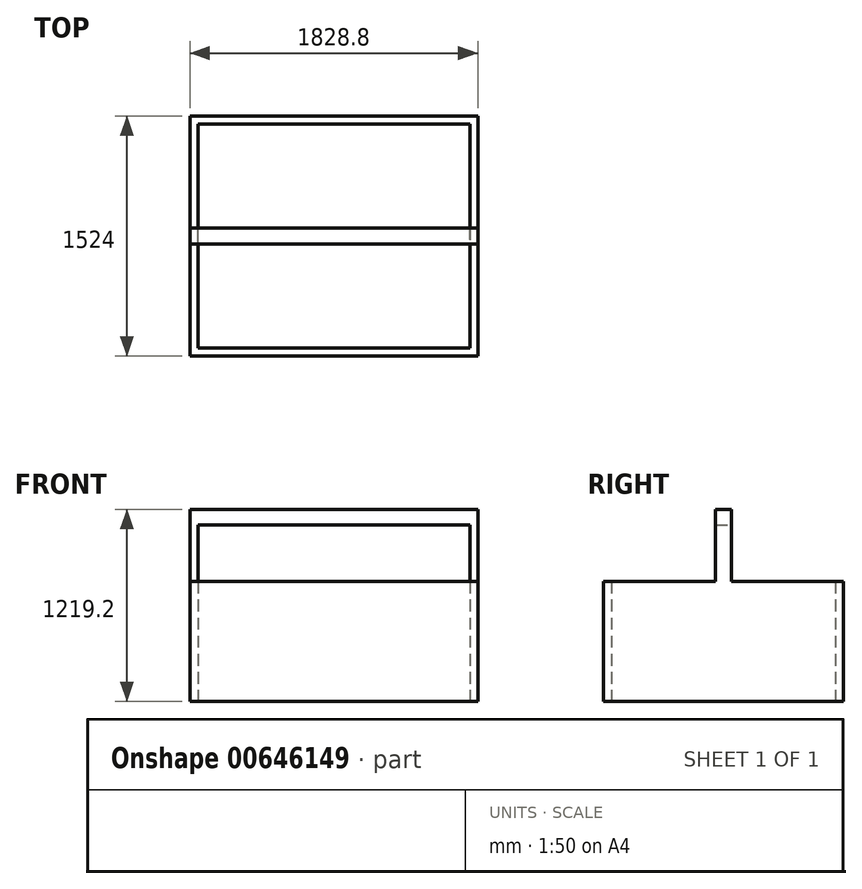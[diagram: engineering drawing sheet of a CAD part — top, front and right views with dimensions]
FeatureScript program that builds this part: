
annotation { "Feature Type Name" : "Feature", "Feature Type Description" : "" }
export const myFeature = defineFeature(function(context is Context, id is Id, definition is map)
    precondition{}
    {
        {
            var Q0;
            Q0=qCreatedBy(makeId("Top.planeOp"),FACE);
            var sketch = newSketch(context, id + "F0", { "sketchPlane" : qUnion([Q0])});
            skLineSegment(sketch, "E0.bottom", {"start": v(-610.33, -745.03) * mm, "end": v(1218.47, -745.03) * mm});
            skLineSegment(sketch, "E0.top", {"start": v(-610.33, 778.97) * mm, "end": v(1218.47, 778.97) * mm});
            skLineSegment(sketch, "E0.left", {"start": v(-610.33, -745.03) * mm, "end": v(-610.33, 778.97) * mm});
            skLineSegment(sketch, "E0.right", {"start": v(1218.47, -745.03) * mm, "end": v(1218.47, 778.97) * mm});
            skLineSegment(sketch, "E1.0", {"start": v(-559.53, 728.17) * mm, "end": v(1167.67, 728.17) * mm});
            skLineSegment(sketch, "E1.1", {"start": v(-559.53, -694.23) * mm, "end": v(-559.53, 728.17) * mm});
            skLineSegment(sketch, "E1.2", {"start": v(-559.53, -694.23) * mm, "end": v(1167.67, -694.23) * mm});
            skLineSegment(sketch, "E1.3", {"start": v(1167.67, -694.23) * mm, "end": v(1167.67, 728.17) * mm});
            skSolve(sketch);
        }
        {
            var Q0;
            Q0=makeQuery(id+"F0.imprint","IMPRINT",FACE,{"disambiguationData":[TD([[makeQuery(id+"F0.imprint","IMPRINT",EDGE,{"derivedFrom":sQuery(id+"F0.wireOp",EDGE,"E0.bottom")}),1.0]])]});
            extrude(context, id + "F1", {"entities" : qUnion([Q0]), "depth" : 762 * mm, "offsetDistance" : 25.4 * mm});
        }
        {
            var Q0;
            Q0=makeQuery(id+"F1.opExtrude","CAP_FACE",FACE,{"disambiguationData":[OSD([sQuery(id+"F0.wireOp",EDGE,"E0.bottom"),sQuery(id+"F0.wireOp",EDGE,"E0.top"),sQuery(id+"F0.wireOp",EDGE,"E0.left"),sQuery(id+"F0.wireOp",EDGE,"E0.right"),sQuery(id+"F0.wireOp",EDGE,"E1.0"),sQuery(id+"F0.wireOp",EDGE,"E1.1"),sQuery(id+"F0.wireOp",EDGE,"E1.2"),sQuery(id+"F0.wireOp",EDGE,"E1.3")])],"isStart":false});
            var sketch = newSketch(context, id + "F2", { "sketchPlane" : qUnion([Q0])});
            skLineSegment(sketch, "E2.bottom", {"start": v(-610.33, 67.77) * mm, "end": v(-559.53, 67.77) * mm});
            skLineSegment(sketch, "E2.top", {"start": v(-610.33, -33.83) * mm, "end": v(-559.53, -33.83) * mm});
            skLineSegment(sketch, "E2.left", {"start": v(-610.33, 67.77) * mm, "end": v(-610.33, -33.83) * mm});
            skLineSegment(sketch, "E2.right", {"start": v(-559.53, 67.77) * mm, "end": v(-559.53, -33.83) * mm});
            skLineSegment(sketch, "E3", {"start": v(304.07, 728.17) * mm, "end": v(304.07, -694.23) * mm, "construction": true});
            skLineSegment(sketch, "E4.MirrorCS", {"start": v(1218.47, -33.83) * mm, "end": v(1167.67, -33.83) * mm});
            skLineSegment(sketch, "E5.MirrorCS", {"start": v(1218.47, 67.77) * mm, "end": v(1167.67, 67.77) * mm});
            skLineSegment(sketch, "E6.MirrorCS", {"start": v(1167.67, 67.77) * mm, "end": v(1167.67, -33.83) * mm});
            skLineSegment(sketch, "E7.MirrorCS", {"start": v(1218.47, 67.77) * mm, "end": v(1218.47, -33.83) * mm});
            skSolve(sketch);
        }
        {
            var Q0;
            Q0 = qSketchRegion(id + "F2", true);
            extrude(context, id + "F3", {"entities" : qUnion([Q0]), "operationType" : NewBodyOperationType.ADD, "depth" : 457.2 * mm, "offsetDistance" : 25.4 * mm});
        }
        {
            var Q0;
            Q0=makeQuery(id+"F3.boolean.opBoolean","MERGE",FACE,{"derivedFrom":[makeQuery(id+"F1.opExtrude","SWEPT_FACE",FACE,{"disambiguationData":[OSD([sQuery(id+"F0.wireOp",EDGE,"E1.1")])]}),makeQuery(id+"F3.opExtrude","SWEPT_FACE",FACE,{"disambiguationData":[OSD([sQuery(id+"F2.wireOp",EDGE,"E2.right")])]})]});
            var sketch = newSketch(context, id + "F4", { "sketchPlane" : qUnion([Q0])});
            skLineSegment(sketch, "E8.bottom", {"start": v(-33.83, 1219.2) * mm, "end": v(67.77, 1219.2) * mm});
            skLineSegment(sketch, "E8.top", {"start": v(-33.83, 1121.81) * mm, "end": v(67.77, 1121.81) * mm});
            skLineSegment(sketch, "E8.left", {"start": v(-33.83, 1219.2) * mm, "end": v(-33.83, 1121.81) * mm});
            skLineSegment(sketch, "E8.right", {"start": v(67.77, 1219.2) * mm, "end": v(67.77, 1121.81) * mm});
            skSolve(sketch);
        }
        {
            var Q0;
            Q0 = qSketchRegion(id + "F4", true);
            extrude(context, id + "F5", {"entities" : qUnion([Q0]), "operationType" : NewBodyOperationType.ADD, "endBound" : BoundingType.UP_TO_NEXT, "depth" : 25.4 * mm, "offsetDistance" : 25.4 * mm});
        }
    });
